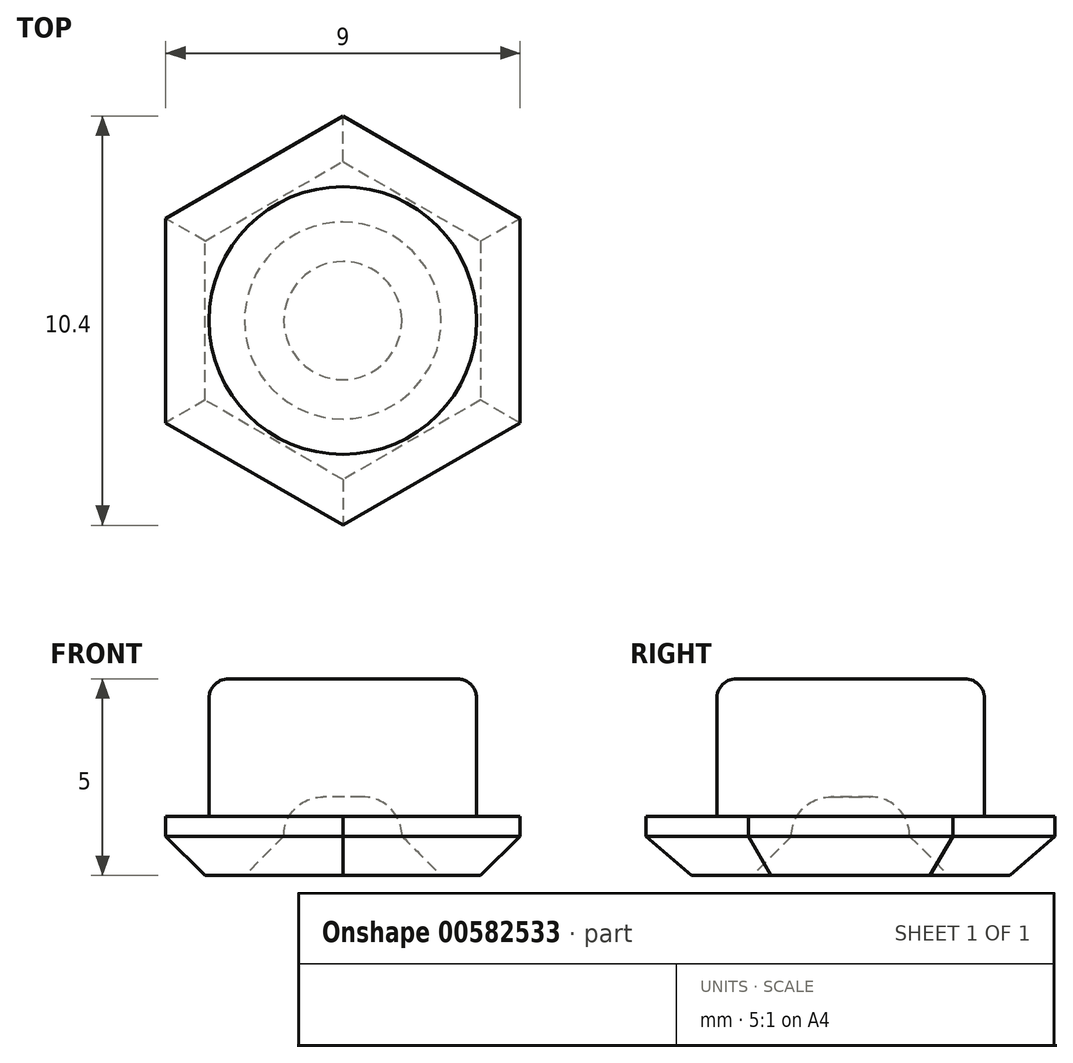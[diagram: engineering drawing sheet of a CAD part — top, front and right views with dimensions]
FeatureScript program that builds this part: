
annotation { "Feature Type Name" : "Feature", "Feature Type Description" : "" }
export const myFeature = defineFeature(function(context is Context, id is Id, definition is map)
    precondition{}
    {
        {
            var Q0;
            Q0=qCreatedBy(makeId("Top.planeOp"),FACE);
            var sketch = newSketch(context, id + "F0", { "sketchPlane" : qUnion([Q0])});
            skCircle(sketch, "E0", {"center": v(0, 0) * mm, "radius": 3.4 * mm});
            skCircle(sketch, "E1.cCircle", {"center": v(0, 0) * mm, "radius": 4.5 * mm, "construction": true});
            skLineSegment(sketch, "E1.0", {"start": v(4.5, 2.6) * mm, "end": v(4.5, -2.6) * mm});
            skLineSegment(sketch, "E1.1", {"start": v(4.5, -2.6) * mm, "end": v(0, -5.2) * mm});
            skLineSegment(sketch, "E1.2", {"start": v(0, -5.2) * mm, "end": v(-4.5, -2.6) * mm});
            skLineSegment(sketch, "E1.3", {"start": v(-4.5, -2.6) * mm, "end": v(-4.5, 2.6) * mm});
            skLineSegment(sketch, "E1.4", {"start": v(-4.5, 2.6) * mm, "end": v(0, 5.2) * mm});
            skLineSegment(sketch, "E1.5", {"start": v(0, 5.2) * mm, "end": v(4.5, 2.6) * mm});
            skPoint(sketch, "E1.0.midPoint", {"position": v(4.5, 0) * mm});
            skCircle(sketch, "E2", {"center": v(0, 0) * mm, "radius": 1.5 * mm});
            skSolve(sketch);
        }
        {
            var Q0;
            Q0=makeQuery(id+"F0.imprint","IMPRINT",FACE,{"disambiguationData":[TD([[makeQuery(id+"F0.imprint","IMPRINT",EDGE,{"derivedFrom":sQuery(id+"F0.wireOp",EDGE,"E0")}),-1.0]])]});
            extrude(context, id + "F1", {"entities" : qUnion([Q0]), "depth" : 1.5 * mm, "offsetDistance" : 25 * mm});
        }
        {
            var Q0;
            Q0=makeQuery(id+"F0.imprint","IMPRINT",FACE,{"disambiguationData":[TD([[makeQuery(id+"F0.imprint","IMPRINT",EDGE,{"derivedFrom":sQuery(id+"F0.wireOp",EDGE,"E0")}),1.0]])]});
            var Q1;
            Q1=makeQuery(id+"F0.imprint","IMPRINT",FACE,{"disambiguationData":[TD([[makeQuery(id+"F0.imprint","IMPRINT",EDGE,{"derivedFrom":sQuery(id+"F0.wireOp",EDGE,"E2")}),1.0]])]});
            extrude(context, id + "F2", {"entities" : qUnion([Q0, Q1]), "operationType" : NewBodyOperationType.ADD, "depth" : 5 * mm, "offsetDistance" : 25 * mm});
        }
        {
            var Q0;
            Q0=makeQuery(id+"F0.imprint","IMPRINT",FACE,{"disambiguationData":[TD([[makeQuery(id+"F0.imprint","IMPRINT",EDGE,{"derivedFrom":sQuery(id+"F0.wireOp",EDGE,"E2")}),1.0]])]});
            extrude(context, id + "F3", {"entities" : qUnion([Q0]), "operationType" : NewBodyOperationType.REMOVE, "depth" : 2 * mm, "offsetDistance" : 25 * mm});
        }
        {
            var Q0;
            {var subQ0=sQuery(id+"F0.wireOp",EDGE,"E0");Q0=makeQuery(id+"F2.boolean.opBoolean","MERGE",FACE,{"derivedFrom":[makeQuery(id+"F1.opExtrude","CAP_FACE",FACE,{"disambiguationData":[OSD([subQ0,sQuery(id+"F0.wireOp",EDGE,"E1.0"),sQuery(id+"F0.wireOp",EDGE,"E1.1"),sQuery(id+"F0.wireOp",EDGE,"E1.2"),sQuery(id+"F0.wireOp",EDGE,"E1.3"),sQuery(id+"F0.wireOp",EDGE,"E1.4"),sQuery(id+"F0.wireOp",EDGE,"E1.5")])],"isStart":true}),makeQuery(id+"F2.opExtrude","CAP_FACE",FACE,{"disambiguationData":[OSD([subQ0])],"isStart":true})]});}
            chamfer(context, id + "F4", {"entities" : qUnion([Q0]), "width" : 1 * mm, "tangentPropagation" : true});
        }
        {
            var Q0;
            Q0=makeQuery(id+"F3.boolean.opBoolean","COPY",EDGE,{"derivedFrom":makeQuery(id+"F3.opExtrude","CAP_EDGE",EDGE,{"disambiguationData":[OSD([sQuery(id+"F0.wireOp",EDGE,"E2")])],"isStart":false})});
            fillet(context, id + "F5", {"entities" : qUnion([Q0]), "radius" : 1 * mm, "tangentPropagation" : true, "allowEdgeOverflow" : false});
        }
        {
            var Q0;
            Q0=makeQuery(id+"F2.opExtrude","CAP_EDGE",EDGE,{"disambiguationData":[OSD([sQuery(id+"F0.wireOp",EDGE,"E0")])],"isStart":false});
            fillet(context, id + "F6", {"entities" : qUnion([Q0]), "radius" : 0.5 * mm, "tangentPropagation" : true, "allowEdgeOverflow" : false});
        }
    });
